# Revit family: Knotenkonsole L mit 1 Strebe 100x152x 4, VA
name_source: partatom
category: HLS-Bauteile
revit_build: Autodesk Revit 2017 (Build: 20190507_1515(x64)
units: mm (PartAtom-declared; Revit-internal decimal feet)

## family parameters
Basisbauteil = Fläche
Beim Laden mit Abzugskörper schneiden = Nein
Bemaßung runder Anschluss = Durchmesser verwenden
Gemeinsam genutzt = Ja
Raumberechnungspunkt = Nein
Teiletyp = Normal

## types (2) — shared parameters
Abmessung = 150 x 100 x 4 mm
Fabrikat = MEFA
Firma = MEFA Befestigungs- und Montagesysteme GmbH
Gewicht = 0.30 kg
Gewicht pro Bauteil = 0.30 kg
Höhe = 150 mm
Kurztext2 = 150 x 100 x 4 mm für Profil 45
Last bei Länge = 120 mm
Länge = 100 mm  [stored 0.328084 ft]
Material = Edelstahl
Mengeneinheit = St
Profiltyp = 45
Stärke = 4 mm  [stored 0.0131234 ft]
Vorgabe-Ansicht = 1219 mm
max. zul. Last F1 = 0.00 kip
max. zul. Last F2 = 0.00 kip
vpe = 1 St

## per-type parameters (varying)
| type | Artikelnummer | EAN | Kurztext1 | Materialname |
| Knotenkonsole L mit 1 Strebe 100x152x 4, V2A | 0803101 | 4250928419286 | Knotenkonsole mit 1 Strebe V2A | V2A |
| Knotenkonsole L mit 1 Strebe 100x152x 4, V4A | 0803102 | 4250928419293 | Knotenkonsole mit 1 Strebe V4A | V4A |

note: [stored X ft] marks values corroborated as IEEE doubles in the binary element streams (Revit-internal decimal feet)
